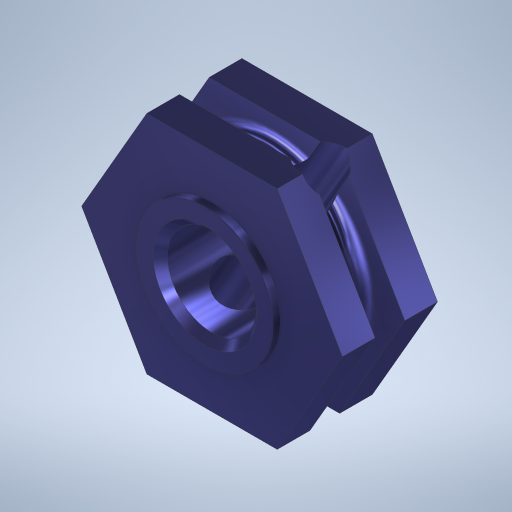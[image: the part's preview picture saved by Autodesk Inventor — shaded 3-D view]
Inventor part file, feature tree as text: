
AUTODESK INVENTOR PART (.ipt)
format: ipt  version: 2023.1 (Build 271208000, 208)  size: 365,568 bytes
history: native  units: in
note: dims shown in document units (in); Inventor stores cm internally (conversion verified against a paired STEP export)
features: extrude x4, sketch x4, plane x2, chamfer x1, revolve x1, projected_geometry x1
ambient origin geometry x8: Origin, YZ Plane, XZ Plane, XY Plane, X Axis, Y Axis, Z Axis, Center Point
bodies: Solid1 (feature_tree)
feature tree (13):
  extrude  "Extrusion1"  Depth=0.2in TaperAngle=0.0deg
  sketch  "Sketch2"  dims[d3=0.1875in d4=0.05in]
  extrude  "Extrusion2"  Depth=0.05in
  extrude  "Extrusion3"  Depth=0.015in TaperAngle=0.0deg
  chamfer  "Chamfer1"  Distance=0.015in Angle=45.0deg
  plane  "Work Plane1"
  extrude  "Extrusion4"  Depth=0.0625in
  plane  "Work Plane2"
  revolve  "Revolution1"  [1 undecoded]
  sketch  "Sketch1"  dims[d0=0.475in d1=0.2in d2=0.0in]
  sketch  "Sketch3"  dims[d5=0.015in d6=0.0in d7=0.015in d8=0.0in d9=0.015in d10=0.125in d11=45.0deg]
  sketch  "Sketch4"  dims[d12=90.0deg d13=0.0938in d14=0.015in d15=0.0in d16=0.0625in d17=0.0625in d18=90.0deg]
  projected_geometry  "Project Cut Edges1"
note: 1 required parameter value undecoded (feature->parameter linkage not recoverable at this tier; creation-order binding heuristic only, values carry confidence <= 0.55)
